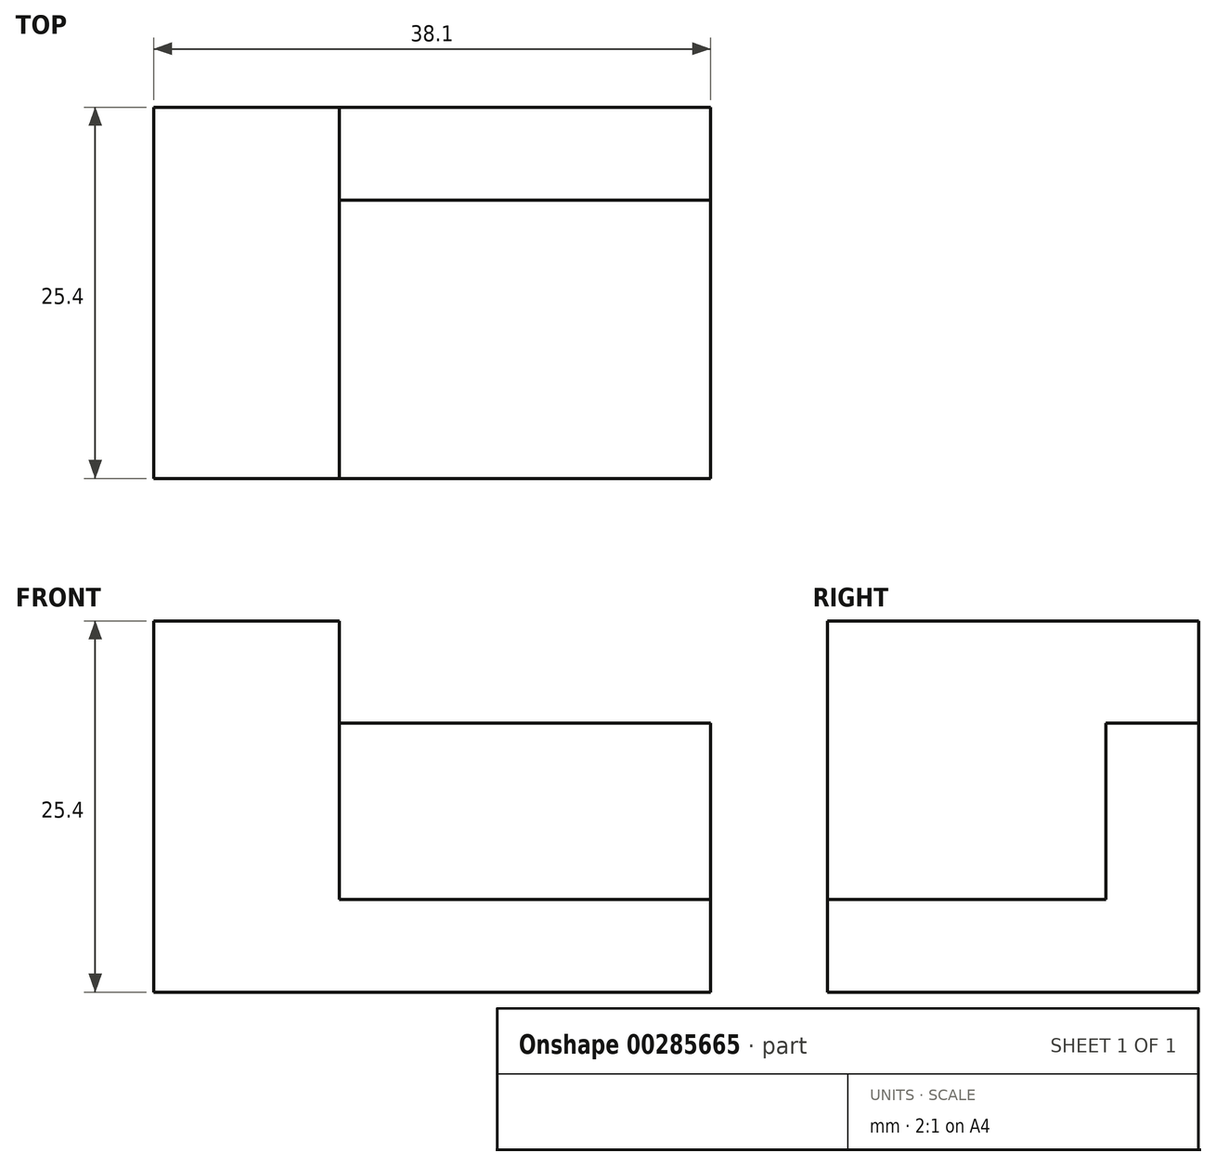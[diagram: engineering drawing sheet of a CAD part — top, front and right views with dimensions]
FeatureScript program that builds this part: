
annotation { "Feature Type Name" : "Feature", "Feature Type Description" : "" }
export const myFeature = defineFeature(function(context is Context, id is Id, definition is map)
    precondition{}
    {
        {
            var Q0;
            Q0=qCreatedBy(makeId("Right.planeOp"),FACE);
            var sketch = newSketch(context, id + "F0", { "sketchPlane" : qUnion([Q0])});
            skLineSegment(sketch, "E0", {"start": v(0, 0) * mm, "end": v(25.4, 0) * mm});
            skLineSegment(sketch, "E1", {"start": v(25.4, 0) * mm, "end": v(25.4, 25.4) * mm});
            skLineSegment(sketch, "E2", {"start": v(25.4, 25.4) * mm, "end": v(0, 25.4) * mm});
            skLineSegment(sketch, "E3", {"start": v(0, 25.4) * mm, "end": v(0, 0) * mm});
            skSolve(sketch);
        }
        {
            var Q0;
            Q0 = qSketchRegion(id + "F0", true);
            extrude(context, id + "F1", {"entities" : qUnion([Q0]), "depth" : 12.7 * mm});
        }
        {
            var Q0;
            Q0=makeQuery(id+"F1.opExtrude","CAP_FACE",FACE,{"disambiguationData":[OSD([sQuery(id+"F0.wireOp",EDGE,"E0"),sQuery(id+"F0.wireOp",EDGE,"E1"),sQuery(id+"F0.wireOp",EDGE,"E2"),sQuery(id+"F0.wireOp",EDGE,"E3")])],"isStart":false});
            var sketch = newSketch(context, id + "F2", { "sketchPlane" : qUnion([Q0])});
            skLineSegment(sketch, "E4", {"start": v(25.4, 0) * mm, "end": v(25.4, 18.41) * mm});
            skLineSegment(sketch, "E5", {"start": v(25.4, 18.41) * mm, "end": v(19.05, 18.41) * mm});
            skLineSegment(sketch, "E6", {"start": v(19.05, 18.41) * mm, "end": v(19.05, 6.35) * mm});
            skLineSegment(sketch, "E7", {"start": v(19.05, 6.35) * mm, "end": v(0, 6.35) * mm});
            skLineSegment(sketch, "E8", {"start": v(0, 6.35) * mm, "end": v(0, 0) * mm});
            skLineSegment(sketch, "E9", {"start": v(0, 0) * mm, "end": v(25.4, 0) * mm});
            skSolve(sketch);
        }
        {
            var Q0;
            Q0 = qSketchRegion(id + "F2", true);
            extrude(context, id + "F3", {"entities" : qUnion([Q0]), "operationType" : NewBodyOperationType.ADD, "depth" : 25.4 * mm});
        }
    });
